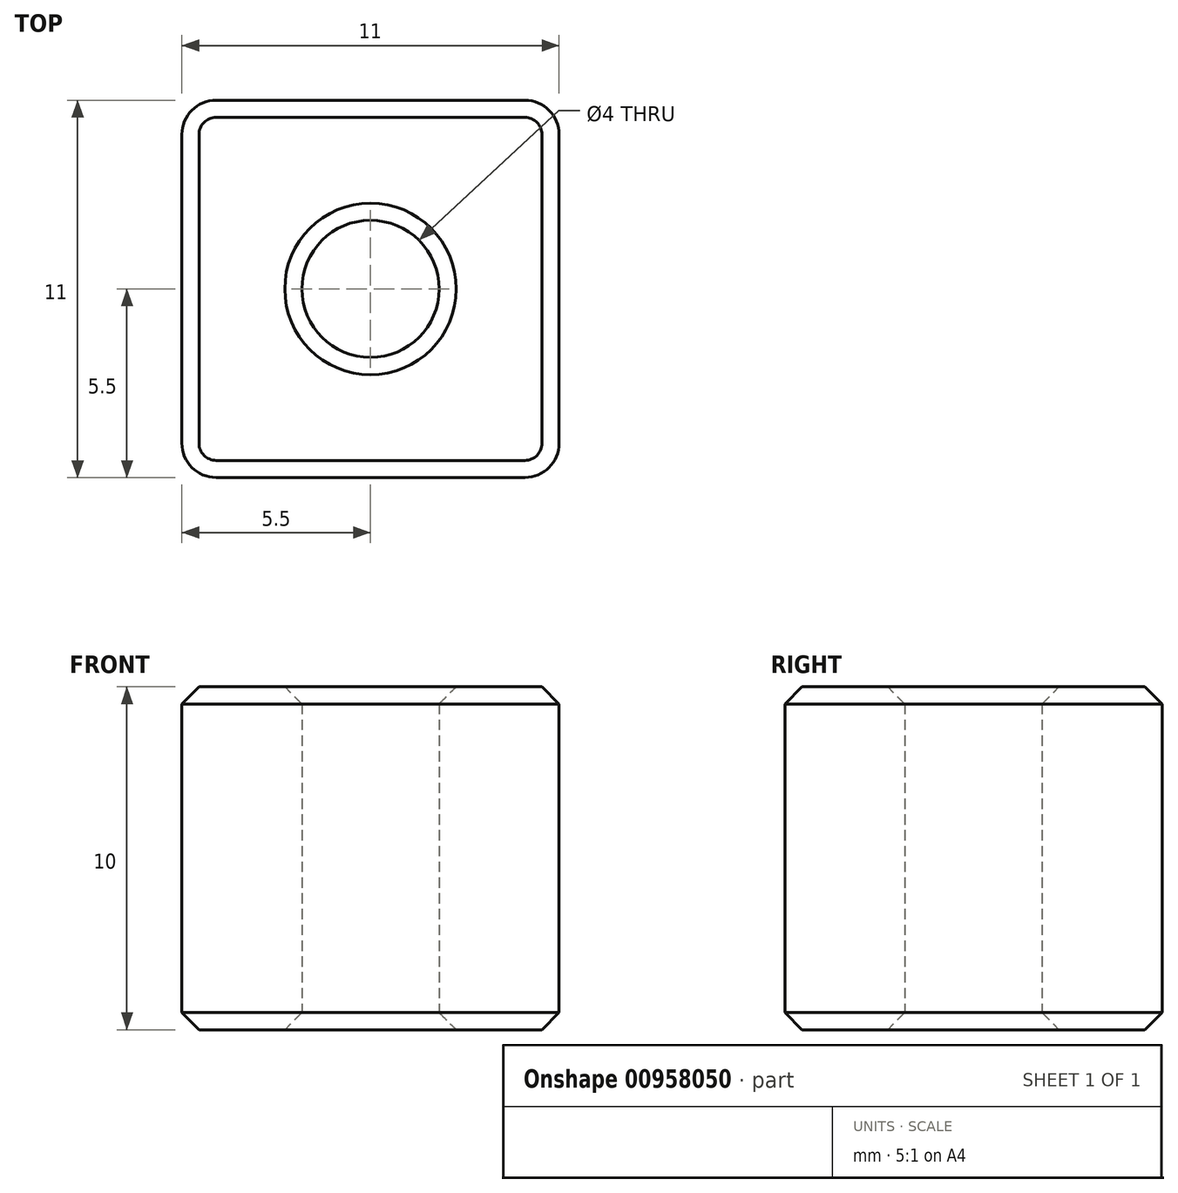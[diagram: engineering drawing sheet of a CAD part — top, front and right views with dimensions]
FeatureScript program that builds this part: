
annotation { "Feature Type Name" : "Feature", "Feature Type Description" : "" }
export const myFeature = defineFeature(function(context is Context, id is Id, definition is map)
    precondition{}
    {
        {
            var Q0;
            Q0=qCreatedBy(makeId("Top.planeOp"),FACE);
            var sketch = newSketch(context, id + "F0", { "sketchPlane" : qUnion([Q0])});
            skLineSegment(sketch, "E0.bottom", {"start": v(4.5, 5.5) * mm, "end": v(-4.5, 5.5) * mm});
            skLineSegment(sketch, "E0.top", {"start": v(4.5, -5.5) * mm, "end": v(-4.5, -5.5) * mm});
            skLineSegment(sketch, "E0.left", {"start": v(5.5, 4.5) * mm, "end": v(5.5, -4.5) * mm});
            skLineSegment(sketch, "E0.right", {"start": v(-5.5, 4.5) * mm, "end": v(-5.5, -4.5) * mm});
            skPoint(sketch, "E0.middle", {"position": v(0, 0) * mm});
            skPoint(sketch, "E1.visualSharp", {"position": v(-5.5, 5.5) * mm});
            skArc(sketch, "E1.filletArc", {"start": v(-4.5, 5.5) * mm, "mid": v(-5.2, 5.2) * mm, "end": v(-5.5, 4.5) * mm});
            skPoint(sketch, "E2.visualSharp", {"position": v(5.5, 5.5) * mm});
            skArc(sketch, "E2.filletArc", {"start": v(5.5, 4.5) * mm, "mid": v(5.2, 5.2) * mm, "end": v(4.5, 5.5) * mm});
            skPoint(sketch, "E3.visualSharp", {"position": v(5.5, -5.5) * mm});
            skArc(sketch, "E3.filletArc", {"start": v(4.5, -5.5) * mm, "mid": v(5.2, -5.2) * mm, "end": v(5.5, -4.5) * mm});
            skPoint(sketch, "E4.visualSharp", {"position": v(-5.5, -5.5) * mm});
            skArc(sketch, "E4.filletArc", {"start": v(-5.5, -4.5) * mm, "mid": v(-5.2, -5.2) * mm, "end": v(-4.5, -5.5) * mm});
            skCircle(sketch, "E5", {"center": v(0, 0) * mm, "radius": 2 * mm});
            skSolve(sketch);
        }
        {
            var Q0;
            Q0=makeQuery(id+"F0.imprint","IMPRINT",FACE,{"disambiguationData":[TD([[makeQuery(id+"F0.imprint","IMPRINT",EDGE,{"derivedFrom":sQuery(id+"F0.wireOp",EDGE,"E0.bottom")}),1.0]])]});
            extrude(context, id + "F1", {"entities" : qUnion([Q0]), "depth" : 10 * mm, "offsetDistance" : 25 * mm});
        }
        {
            var Q0;
            Q0=makeQuery(id+"F1.opExtrude","CAP_FACE",FACE,{"disambiguationData":[OSD([sQuery(id+"F0.wireOp",EDGE,"E0.bottom"),sQuery(id+"F0.wireOp",EDGE,"E0.top"),sQuery(id+"F0.wireOp",EDGE,"E0.left"),sQuery(id+"F0.wireOp",EDGE,"E0.right"),sQuery(id+"F0.wireOp",EDGE,"E1.filletArc"),sQuery(id+"F0.wireOp",EDGE,"E2.filletArc"),sQuery(id+"F0.wireOp",EDGE,"E3.filletArc"),sQuery(id+"F0.wireOp",EDGE,"E4.filletArc"),sQuery(id+"F0.wireOp",EDGE,"E5")])],"isStart":true});
            var Q1;
            Q1=makeQuery(id+"F1.opExtrude","CAP_FACE",FACE,{"disambiguationData":[OSD([sQuery(id+"F0.wireOp",EDGE,"E0.bottom"),sQuery(id+"F0.wireOp",EDGE,"E0.top"),sQuery(id+"F0.wireOp",EDGE,"E0.left"),sQuery(id+"F0.wireOp",EDGE,"E0.right"),sQuery(id+"F0.wireOp",EDGE,"E1.filletArc"),sQuery(id+"F0.wireOp",EDGE,"E2.filletArc"),sQuery(id+"F0.wireOp",EDGE,"E3.filletArc"),sQuery(id+"F0.wireOp",EDGE,"E4.filletArc"),sQuery(id+"F0.wireOp",EDGE,"E5")])],"isStart":false});
            chamfer(context, id + "F2", {"entities" : qUnion([Q0, Q1]), "width" : 0.5 * mm, "tangentPropagation" : true});
        }
    });
